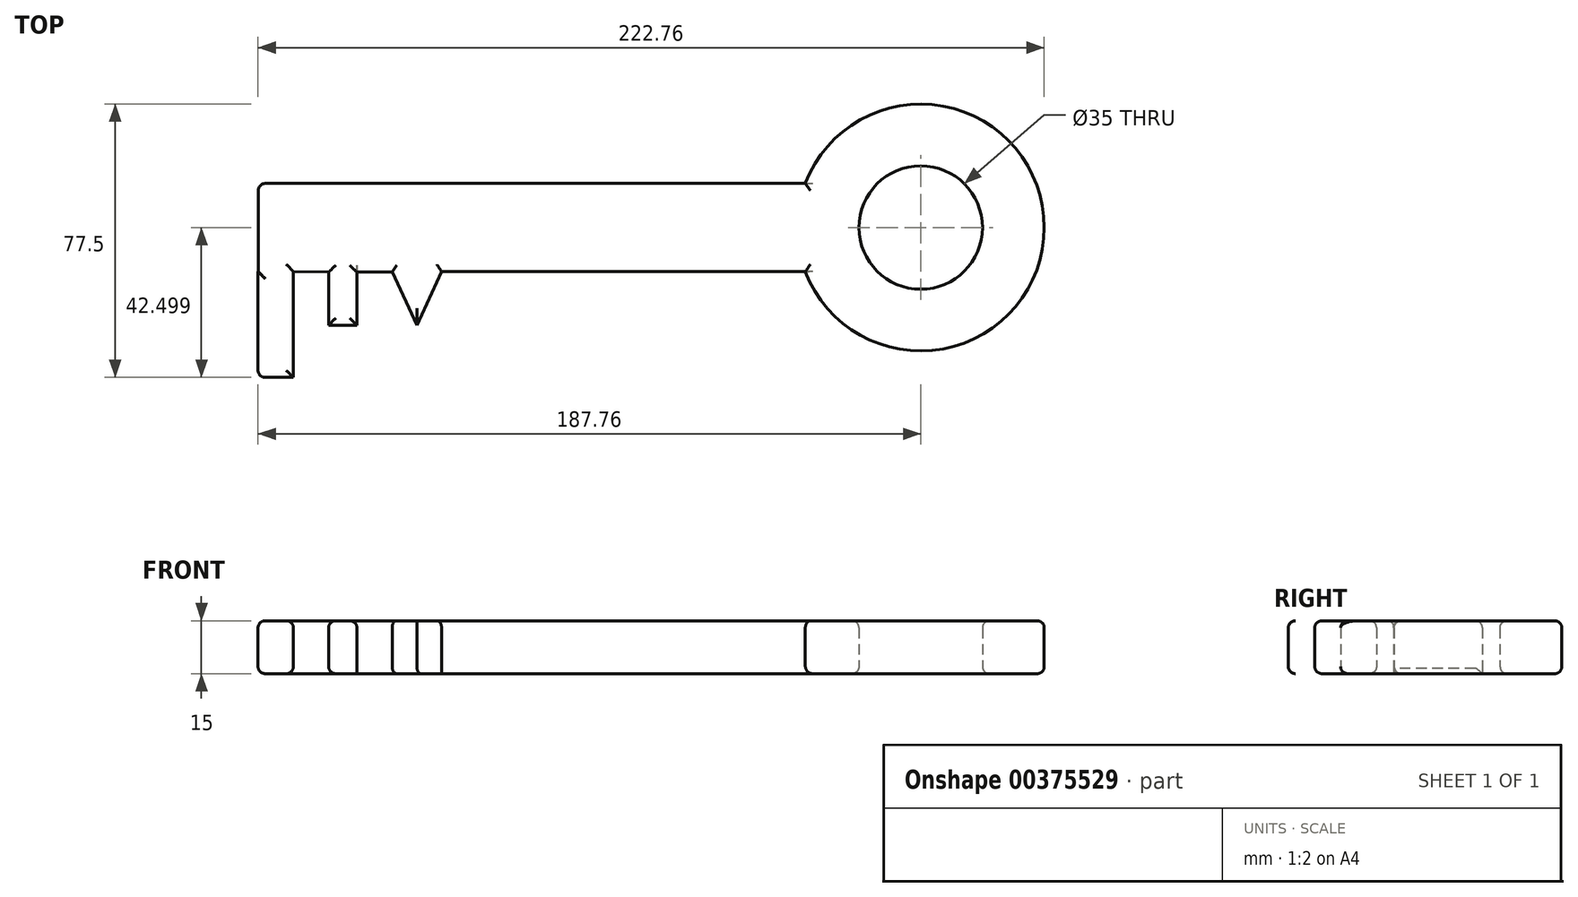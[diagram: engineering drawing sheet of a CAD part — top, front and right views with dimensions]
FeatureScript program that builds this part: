
annotation { "Feature Type Name" : "Feature", "Feature Type Description" : "" }
export const myFeature = defineFeature(function(context is Context, id is Id, definition is map)
    precondition{}
    {
        {
            var Q0;
            Q0=qCreatedBy(makeId("Top.planeOp"),FACE);
            var sketch = newSketch(context, id + "F0", { "sketchPlane" : qUnion([Q0])});
            skLineSegment(sketch, "E0.bottom", {"start": v(-102.41, 43.74) * mm, "end": v(-102.34, 43.74) * mm});
            skLineSegment(sketch, "E0.top", {"start": v(-102.41, 13.74) * mm, "end": v(-92.41, 13.74) * mm});
            skLineSegment(sketch, "E0.left", {"start": v(-102.41, 43.74) * mm, "end": v(-102.41, 13.74) * mm});
            skLineSegment(sketch, "E0.right", {"start": v(-92.41, 43.74) * mm, "end": v(-92.41, 13.74) * mm});
            skLineSegment(sketch, "E1.top", {"start": v(-82.41, 28.56) * mm, "end": v(-74.41, 28.56) * mm});
            skLineSegment(sketch, "E1.left", {"start": v(-82.41, 43.56) * mm, "end": v(-82.41, 28.56) * mm});
            skLineSegment(sketch, "E1.right", {"start": v(-74.41, 43.56) * mm, "end": v(-74.41, 28.56) * mm});
            skPoint(sketch, "E2.oppositeSnap0", {"position": v(-92.41, 28.74) * mm});
            skLineSegment(sketch, "E3.bottom", {"start": v(-102.34, 68.74) * mm, "end": v(52.66, 68.74) * mm});
            skLineSegment(sketch, "E3.left", {"start": v(-102.34, 68.74) * mm, "end": v(-102.34, 43.74) * mm});
            skLineSegment(sketch, "E4", {"start": v(-64.41, 43.56) * mm, "end": v(-57.42, 28.56) * mm});
            skLineSegment(sketch, "E5", {"start": v(-57.42, 28.56) * mm, "end": v(-50.41, 43.74) * mm});
            skArc(sketch, "E6", {"start": v(52.66, 43.74) * mm, "mid": v(120.35, 56.24) * mm, "end": v(52.66, 68.74) * mm});
            skCircle(sketch, "E7", {"center": v(85.35, 56.24) * mm, "radius": 17.5 * mm});
            skLineSegment(sketch, "E8", {"start": v(67.85, 56.24) * mm, "end": v(85.35, 56.24) * mm});
            skLineSegment(sketch, "E9.trimOffspring", {"start": v(-50.41, 43.74) * mm, "end": v(52.66, 43.74) * mm});
            skPoint(sketch, "E10.orphan", {"position": v(-102.34, 56.24) * mm});
            skLineSegment(sketch, "E11", {"start": v(-102.34, 56.24) * mm, "end": v(85.35, 56.24) * mm, "construction": true});
            skLineSegment(sketch, "E12", {"start": v(-92.41, 43.74) * mm, "end": v(-82.41, 43.56) * mm});
            skLineSegment(sketch, "E13", {"start": v(-74.41, 43.56) * mm, "end": v(-64.41, 43.56) * mm});
            skSolve(sketch);
        }
        {
            var Q0;
            Q0=makeQuery(id+"F0.imprint","IMPRINT",FACE,{"disambiguationData":[TD([[makeQuery(id+"F0.imprint","IMPRINT",EDGE,{"derivedFrom":sQuery(id+"F0.wireOp",EDGE,"E0.bottom")}),-1.0]])]});
            extrude(context, id + "F1", {"entities" : qUnion([Q0]), "depth" : 15 * mm});
        }
        {
            var Q0;
            Q0=makeQuery(id+"F1.opExtrude","CAP_EDGE",EDGE,{"disambiguationData":[OSD([sQuery(id+"F0.wireOp",EDGE,"E3.bottom")])],"isStart":false});
            var Q1;
            Q1=makeQuery(id+"F1.opExtrude","CAP_EDGE",EDGE,{"disambiguationData":[OSD([sQuery(id+"F0.wireOp",EDGE,"E3.left")])],"isStart":false});
            var Q2;
            Q2=makeQuery(id+"F1.opExtrude","CAP_EDGE",EDGE,{"disambiguationData":[OSD([sQuery(id+"F0.wireOp",EDGE,"E0.left")])],"isStart":false});
            var Q3;
            Q3=makeQuery(id+"F1.opExtrude","CAP_EDGE",EDGE,{"disambiguationData":[OSD([sQuery(id+"F0.wireOp",EDGE,"E0.right")])],"isStart":false});
            var Q4;
            Q4=makeQuery(id+"F1.opExtrude","CAP_EDGE",EDGE,{"disambiguationData":[OSD([sQuery(id+"F0.wireOp",EDGE,"E1.left")])],"isStart":false});
            var Q5;
            Q5=makeQuery(id+"F1.opExtrude","CAP_EDGE",EDGE,{"disambiguationData":[OSD([sQuery(id+"F0.wireOp",EDGE,"E12")])],"isStart":false});
            var Q6;
            Q6=makeQuery(id+"F1.opExtrude","CAP_FACE",FACE,{"disambiguationData":[OSD([sQuery(id+"F0.wireOp",EDGE,"E0.bottom"),sQuery(id+"F0.wireOp",EDGE,"E0.top"),sQuery(id+"F0.wireOp",EDGE,"E0.left"),sQuery(id+"F0.wireOp",EDGE,"E0.right"),sQuery(id+"F0.wireOp",EDGE,"E1.top"),sQuery(id+"F0.wireOp",EDGE,"E1.left"),sQuery(id+"F0.wireOp",EDGE,"E1.right"),sQuery(id+"F0.wireOp",EDGE,"E3.bottom"),sQuery(id+"F0.wireOp",EDGE,"E3.left"),sQuery(id+"F0.wireOp",EDGE,"E4"),sQuery(id+"F0.wireOp",EDGE,"E5"),sQuery(id+"F0.wireOp",EDGE,"E6"),sQuery(id+"F0.wireOp",EDGE,"E7"),sQuery(id+"F0.wireOp",EDGE,"E9.trimOffspring"),sQuery(id+"F0.wireOp",EDGE,"E12"),sQuery(id+"F0.wireOp",EDGE,"E13")])],"isStart":false});
            var Q7;
            Q7=makeQuery(id+"F1.opExtrude","CAP_EDGE",EDGE,{"disambiguationData":[OSD([sQuery(id+"F0.wireOp",EDGE,"E1.right")])],"isStart":false});
            var Q8;
            Q8=makeQuery(id+"F1.opExtrude","CAP_EDGE",EDGE,{"disambiguationData":[OSD([sQuery(id+"F0.wireOp",EDGE,"E13")])],"isStart":false});
            var Q9;
            Q9=makeQuery(id+"F1.opExtrude","CAP_EDGE",EDGE,{"disambiguationData":[OSD([sQuery(id+"F0.wireOp",EDGE,"E4")])],"isStart":false});
            var Q10;
            Q10=makeQuery(id+"F1.opExtrude","CAP_EDGE",EDGE,{"disambiguationData":[OSD([sQuery(id+"F0.wireOp",EDGE,"E9.trimOffspring")])],"isStart":false});
            var Q11;
            Q11=makeQuery(id+"F1.opExtrude","CAP_EDGE",EDGE,{"disambiguationData":[OSD([sQuery(id+"F0.wireOp",EDGE,"E6")])],"isStart":false});
            var Q12;
            Q12=makeQuery(id+"F1.opExtrude","CAP_EDGE",EDGE,{"disambiguationData":[OSD([sQuery(id+"F0.wireOp",EDGE,"E7")])],"isStart":false});
            var Q13;
            Q13=makeQuery(id+"F1.opExtrude","SWEPT_EDGE",EDGE,{"disambiguationData":[OSD([sQuery(id+"F0.wireOp",EDGE,"E3.bottom"),sQuery(id+"F0.wireOp",EDGE,"E3.left")])]});
            var Q14;
            Q14=makeQuery(id+"F1.opExtrude","SWEPT_EDGE",EDGE,{"disambiguationData":[OSD([sQuery(id+"F0.wireOp",EDGE,"E0.top"),sQuery(id+"F0.wireOp",EDGE,"E0.left")])]});
            var Q15;
            Q15=makeQuery(id+"F1.opExtrude","CAP_EDGE",EDGE,{"disambiguationData":[OSD([sQuery(id+"F0.wireOp",EDGE,"E12")])],"isStart":true});
            var Q16;
            Q16=makeQuery(id+"F1.opExtrude","CAP_EDGE",EDGE,{"disambiguationData":[OSD([sQuery(id+"F0.wireOp",EDGE,"E0.right")])],"isStart":true});
            var Q17;
            Q17=makeQuery(id+"F1.opExtrude","CAP_EDGE",EDGE,{"disambiguationData":[OSD([sQuery(id+"F0.wireOp",EDGE,"E0.top")])],"isStart":true});
            var Q18;
            Q18=makeQuery(id+"F1.opExtrude","CAP_EDGE",EDGE,{"disambiguationData":[OSD([sQuery(id+"F0.wireOp",EDGE,"E0.left")])],"isStart":true});
            var Q19;
            Q19=makeQuery(id+"F1.opExtrude","CAP_EDGE",EDGE,{"disambiguationData":[OSD([sQuery(id+"F0.wireOp",EDGE,"E1.left")])],"isStart":true});
            var Q20;
            Q20=makeQuery(id+"F1.opExtrude","CAP_EDGE",EDGE,{"disambiguationData":[OSD([sQuery(id+"F0.wireOp",EDGE,"E1.top")])],"isStart":true});
            var Q21;
            Q21=makeQuery(id+"F1.opExtrude","CAP_EDGE",EDGE,{"disambiguationData":[OSD([sQuery(id+"F0.wireOp",EDGE,"E13")])],"isStart":true});
            var Q22;
            Q22=makeQuery(id+"F1.opExtrude","CAP_EDGE",EDGE,{"disambiguationData":[OSD([sQuery(id+"F0.wireOp",EDGE,"E4")])],"isStart":true});
            var Q23;
            Q23=makeQuery(id+"F1.opExtrude","CAP_EDGE",EDGE,{"disambiguationData":[OSD([sQuery(id+"F0.wireOp",EDGE,"E6")])],"isStart":true});
            var Q24;
            Q24=makeQuery(id+"F1.opExtrude","CAP_EDGE",EDGE,{"disambiguationData":[OSD([sQuery(id+"F0.wireOp",EDGE,"E7")])],"isStart":true});
            fillet(context, id + "F2", {"entities" : qUnion([Q0, Q1, Q2, Q3, Q4, Q5, Q6, Q7, Q8, Q9, Q10, Q11, Q12, Q13, Q14, Q15, Q16, Q17, Q18, Q19, Q20, Q21, Q22, Q23, Q24]), "radius" : 2 * mm, "tangentPropagation" : true, "allowEdgeOverflow" : false});
        }
    });
